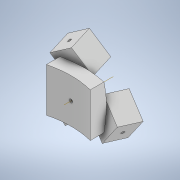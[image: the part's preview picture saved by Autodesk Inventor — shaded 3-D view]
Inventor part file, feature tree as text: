
AUTODESK INVENTOR PART (.ipt)
format: ipt  version: 2022 (Build 260153000, 153)  size: 235,008 bytes
history: native  units: mm
features: sketch x8, extrude x7, pattern_circular x6, revolve x1, plane x1
ambient origin geometry x8: Origin, YZ Plane, XZ Plane, XY Plane, X Axis, Y Axis, Z Axis, Center Point
bodies: Body1 (feature_tree), Body2 (feature_tree)
feature tree (23):
  extrude  "Extrusion3"  Depth=10.0mm
  revolve  "Revolution1"  [1 undecoded]
  plane  "Work Plane1"
  extrude  "Extrusion4"  TaperAngle=90.0deg  [1 undecoded]
  pattern_circular  "Circular Pattern1"  Count=2  [1 undecoded]
  pattern_circular  "Circular Pattern2"  Count=2  [1 undecoded]
  extrude  "Extrusion5"  Depth=5.0mm
  extrude  "Extrusion6"  Depth=10.0mm TaperAngle=0.0deg
  pattern_circular  "Circular Pattern3"  [2 undecoded]
  pattern_circular  "Circular Pattern4"  Count=2  [1 undecoded]
  extrude  "Extrusion7"  Depth=20.0mm
  pattern_circular  "Circular Pattern5"  [2 undecoded]
  pattern_circular  "Circular Pattern6"  [2 undecoded]
  extrude  "Extrusion8"  Depth=10.0mm
  extrude  "Extrusion9"  TaperAngle=0.0deg  [1 undecoded]
  sketch  "Sketch3"  dims[d7=10.0mm d8=10.0mm]
  sketch  "Sketch8"  dims[d9=10.0mm d10=0.0mm d13=13.108049mm]
  sketch  "Sketch9"  dims[d14=15.0deg d15=90.0deg]
  sketch  "Sketch10"  dims[d16=0.75mm]
  sketch  "Sketch11"  dims[d17=2.0mm]
  sketch  "Sketch12"  dims[d18=2.0mm d19=0.0mm d20=20.0mm d21=45.378561mm d23=20.0mm d24=-45.378561mm]
  sketch  "Sketch13"  dims[d26=5.0mm d27=5.0mm]
  sketch  "Sketch14"  dims[d28=0.5mm d29=5.0mm d30=0.0mm d31=0.5mm d32=0.0mm d33=20.0mm d34=45.378561mm d36=20.0mm d37=-45.378561mm d39=0.75mm d40=2.0mm d41=2.5mm d42=0.0mm d43=0.0mm d44=20.0mm d45=45.378561mm d47=20.0mm d48=-45.378561mm d50=40.0mm d51=10.0mm d52=0.0mm d53=0.75mm d54=0.0mm d55=0.0mm]
note: 12 required parameter values undecoded (feature->parameter linkage not recoverable at this tier; creation-order binding heuristic only, values carry confidence <= 0.55)